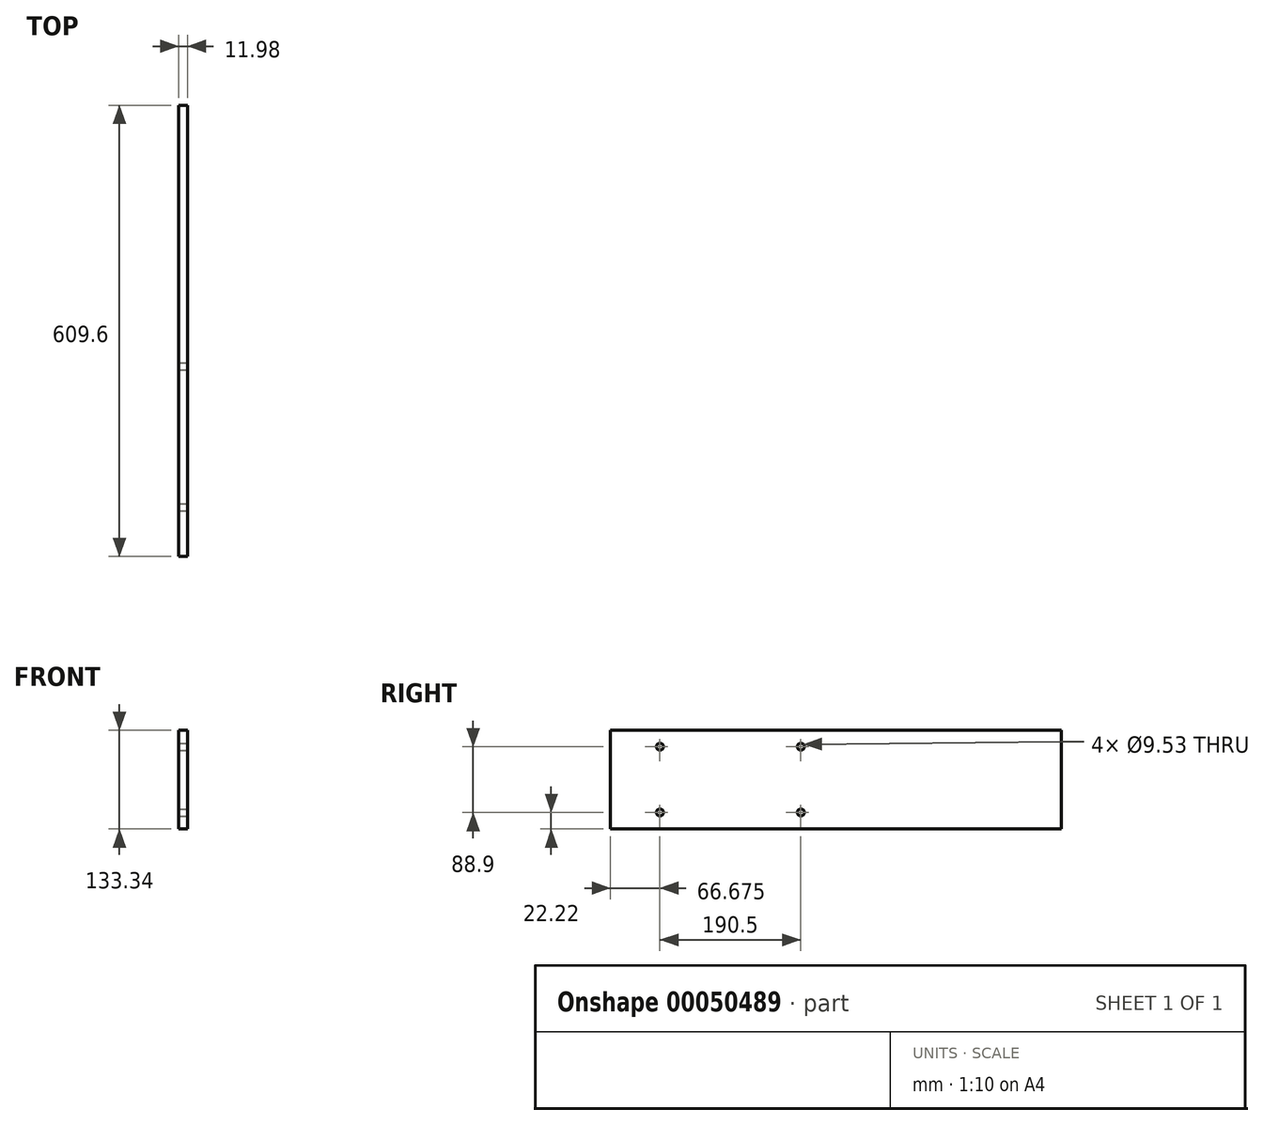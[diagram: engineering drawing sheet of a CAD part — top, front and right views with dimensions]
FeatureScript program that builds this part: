
annotation { "Feature Type Name" : "Feature", "Feature Type Description" : "" }
export const myFeature = defineFeature(function(context is Context, id is Id, definition is map)
    precondition{}
    {
        {
            var Q0;
            Q0=qCreatedBy(makeId("Right.planeOp"),FACE);
            var sketch = newSketch(context, id + "F0", { "sketchPlane" : qUnion([Q0])});
            skLineSegment(sketch, "E0.rect.bottom", {"start": v(304.8, -66.67) * mm, "end": v(-304.8, -66.67) * mm});
            skLineSegment(sketch, "E0.rect.top", {"start": v(304.8, 66.68) * mm, "end": v(-304.8, 66.67) * mm});
            skLineSegment(sketch, "E0.rect.left", {"start": v(304.8, -66.67) * mm, "end": v(304.8, 66.68) * mm});
            skLineSegment(sketch, "E0.rect.right", {"start": v(-304.8, -66.67) * mm, "end": v(-304.8, 66.68) * mm});
            skPoint(sketch, "E0.rect.middle", {"position": v(0, 0) * mm});
            skSolve(sketch);
        }
        {
            var Q0;
            Q0=qSketchRegion(id+"F0",true);
            extrude(context, id + "F1", {"entities" : qUnion([Q0]), "endBound" : BoundingType.SYMMETRIC, "depth" : 12 * mm});
        }
        {
            var Q0;
            Q0=makeQuery(id+"F1.opExtrude","CAP_FACE",FACE,{"disambiguationData":[OSD([sQuery(id+"F0.wireOp",EDGE,"E0.rect.bottom"),sQuery(id+"F0.wireOp",EDGE,"E0.rect.top"),sQuery(id+"F0.wireOp",EDGE,"E0.rect.left"),sQuery(id+"F0.wireOp",EDGE,"E0.rect.right")])],"isStart":false});
            var sketch = newSketch(context, id + "F2", { "sketchPlane" : qUnion([Q0])});
            skLineSegment(sketch, "E1.bottom", {"start": v(-238.12, 44.45) * mm, "end": v(-47.62, 44.45) * mm, "construction": true});
            skLineSegment(sketch, "E1.top", {"start": v(-238.12, -44.45) * mm, "end": v(-47.62, -44.45) * mm, "construction": true});
            skLineSegment(sketch, "E1.left", {"start": v(-238.13, 44.45) * mm, "end": v(-238.12, -44.45) * mm, "construction": true});
            skLineSegment(sketch, "E1.right", {"start": v(-47.63, 44.45) * mm, "end": v(-47.62, -44.45) * mm, "construction": true});
            skCircle(sketch, "E2", {"center": v(-238.12, -44.45) * mm, "radius": 4.76 * mm});
            skCircle(sketch, "E3", {"center": v(-47.62, -44.45) * mm, "radius": 4.76 * mm});
            skCircle(sketch, "E4", {"center": v(-47.62, 44.45) * mm, "radius": 4.76 * mm});
            skCircle(sketch, "E5", {"center": v(-238.12, 44.45) * mm, "radius": 4.76 * mm});
            skLineSegment(sketch, "E6", {"start": v(-238.12, 0) * mm, "end": v(0, 0) * mm, "construction": true});
            skSolve(sketch);
        }
        {
            var Q0;
            Q0 = qSketchRegion(id + "F2", true);
            extrude(context, id + "F3", {"entities" : qUnion([Q0]), "operationType" : NewBodyOperationType.REMOVE, "endBound" : BoundingType.UP_TO_NEXT, "oppositeDirection" : true, "depth" : 25.4 * mm});
        }
    });
